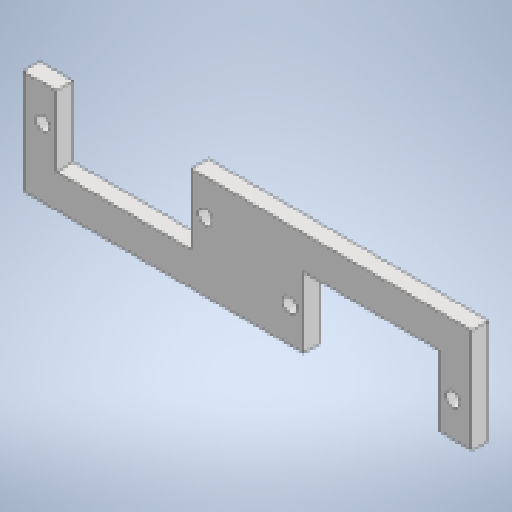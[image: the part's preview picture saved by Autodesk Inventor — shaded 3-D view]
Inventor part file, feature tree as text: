
AUTODESK INVENTOR PART (.ipt)
format: ipt  version: 2023 (Build 270158000, 158)  size: 166,912 bytes
history: native  units: mm
features: extrude x2, sketch x2, other x1, projected_geometry x1
ambient origin geometry x8: Origin, YZ Plane, XZ Plane, XY Plane, X Axis, Y Axis, Z Axis, Center Point
bodies: Body1 (feature_tree)
feature tree (6):
  other  "實體1"
  extrude  "擠出1"  Depth=24.0mm
  extrude  "擠出2"  Depth=12.5mm
  sketch  "草圖1"
  sketch  "草圖2"
  projected_geometry  "投影迴路1"
